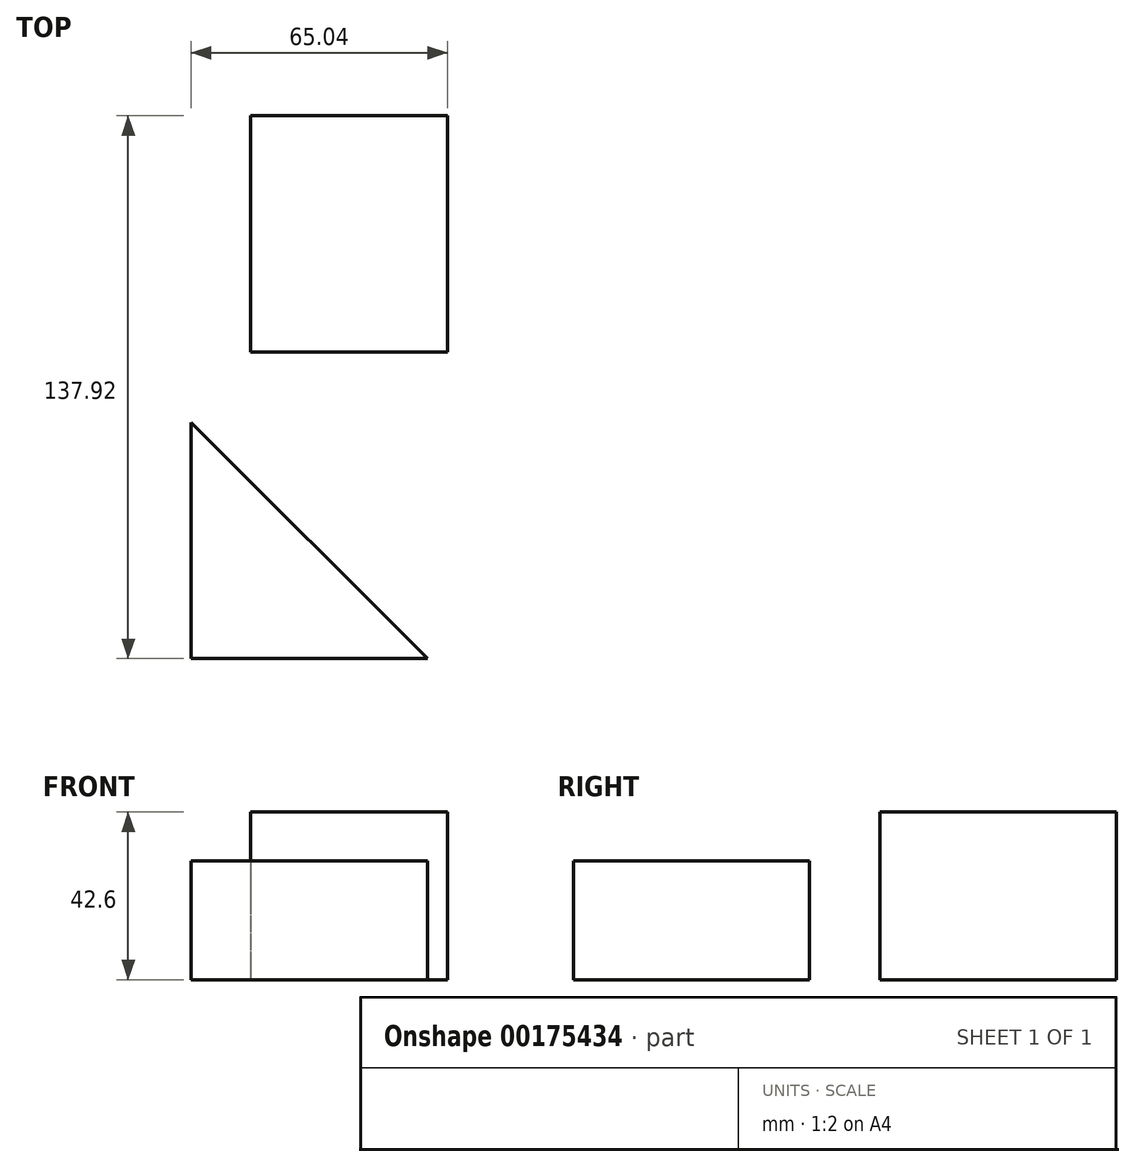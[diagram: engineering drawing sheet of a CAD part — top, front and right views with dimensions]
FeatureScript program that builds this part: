
annotation { "Feature Type Name" : "Feature", "Feature Type Description" : "" }
export const myFeature = defineFeature(function(context is Context, id is Id, definition is map)
    precondition{}
    {
        {
            var Q0;
            Q0=qCreatedBy(makeId("Top.planeOp"),FACE);
            var sketch = newSketch(context, id + "F0", { "sketchPlane" : qUnion([Q0])});
            skLineSegment(sketch, "E0.bottom", {"start": v(-35.97, 70.04) * mm, "end": v(14.03, 70.04) * mm});
            skLineSegment(sketch, "E0.top", {"start": v(-35.97, 10.04) * mm, "end": v(14.03, 10.04) * mm});
            skLineSegment(sketch, "E0.left", {"start": v(-35.97, 70.04) * mm, "end": v(-35.97, 10.04) * mm});
            skLineSegment(sketch, "E0.right", {"start": v(14.03, 70.04) * mm, "end": v(14.03, 10.04) * mm});
            skSolve(sketch);
        }
        {
            var Q0;
            Q0=makeQuery(id+"F0.imprint","IMPRINT",FACE,{"disambiguationData":[TD([[makeQuery(id+"F0.imprint","IMPRINT",EDGE,{"derivedFrom":sQuery(id+"F0.wireOp",EDGE,"E0.bottom")}),-1.0]])]});
            extrude(context, id + "F1", {"entities" : qUnion([Q0]), "depth" : 42.6 * mm});
        }
        {
            var Q0;
            Q0=qCreatedBy(makeId("Top.planeOp"),FACE);
            var sketch = newSketch(context, id + "F2", { "sketchPlane" : qUnion([Q0])});
            skLineSegment(sketch, "E1", {"start": v(-51.01, -7.88) * mm, "end": v(-51.01, -67.88) * mm});
            skLineSegment(sketch, "E2", {"start": v(-51.01, -67.88) * mm, "end": v(8.99, -67.88) * mm});
            skLineSegment(sketch, "E3", {"start": v(8.99, -67.88) * mm, "end": v(-51.01, -7.88) * mm});
            skSolve(sketch);
        }
        {
            var Q0;
            Q0=makeQuery(id+"F2.imprint","IMPRINT",FACE,{"disambiguationData":[TD([[makeQuery(id+"F2.imprint","IMPRINT",EDGE,{"derivedFrom":sQuery(id+"F2.wireOp",EDGE,"E1")}),1.0]])]});
            extrude(context, id + "F3", {"entities" : qUnion([Q0]), "depth" : 30.2 * mm});
        }
    });
